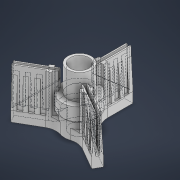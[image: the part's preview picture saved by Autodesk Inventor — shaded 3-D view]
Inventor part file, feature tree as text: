
AUTODESK INVENTOR PART (.ipt)
format: ipt  version: 2022 (Build 260153000, 153)  size: 952,320 bytes
history: native  units: in
note: dims shown in document units (in); Inventor stores cm internally (conversion verified against a paired STEP export)
features: projected_geometry x17, sketch x15, extrude x13, pattern_circular x2, chamfer x1, pattern_linear x1, plane x1, fillet x1
ambient origin geometry x8: Origin, YZ Plane, XZ Plane, XY Plane, X Axis, Y Axis, Z Axis, Center Point
bodies: Solid1 (feature_tree)
feature tree (51):
  extrude  "Extrusion1"  Depth=0.55in
  extrude  "Extrusion2"  Depth=0.125in TaperAngle=0.0deg
  extrude  "Extrusion3"  Depth=0.375in TaperAngle=0.0deg
  extrude  "Extrusion4"  Depth=0.15in
  sketch  "Sketch5"  dims[d11=0.0in d12=1.0in d13=0.0in]
  extrude  "Extrusion5"  Depth=1.0in TaperAngle=0.0deg
  chamfer  "Chamfer1"  Distance=1.0in
  sketch  "Sketch7"  dims[d17=0.08in d18=0.125in d19=45.0deg d20=1.0in]
  extrude  "Extrusion7"  Depth=1.0in
  extrude  "Extrusion8"  Depth=0.25in TaperAngle=0.0deg
  pattern_linear  "Rectangular Pattern1"  Count1=4 Spacing1=0.25in
  plane  "Work Plane1"
  fillet  "Fillet1"  Radius=0.5in
  pattern_circular  "Circular Pattern1"  Count=3 Angle=360.0deg
  extrude  "Extrusion10"  Depth=0.25in TaperAngle=0.0deg
  extrude  "Extrusion11"  Depth=0.125in
  extrude  "Extrusion12"  Depth=0.15in TaperAngle=360.0deg
  extrude  "Extrusion13"  Depth=0.25in TaperAngle=0.0deg
  sketch  "Sketch14"  dims[d56=0.3in d57=0.0in d58=0.25in d59=0.0in]
  pattern_circular  "Circular Pattern3"  [2 undecoded]
  extrude  "Extrusion14"  [1 undecoded]
  extrude  "Extrusion15"  [1 undecoded]
  sketch  "Sketch1"  dims[d0=0.69in d1=0.55in]
  sketch  "Sketch2"  dims[d2=1.0in d3=0.0in d4=0.125in d5=0.0in]
  sketch  "Sketch3"  dims[d6=0.875in d7=0.375in d8=0.0in]
  sketch  "Sketch4"  dims[d9=1.4375in d10=0.15in]
  projected_geometry  "Projected Loop1"
  sketch  "Sketch6"  dims[d14=0.0714in d15=1.0in d16=0.0in]
  projected_geometry  "Projected Loop2"
  sketch  "Sketch8"  dims[d23=0.25in d24=0.125in d25=0.0in]
  projected_geometry  "Projected Loop3"
  sketch  "Sketch9"  dims[d26=0.125in d27=0.0in d28=1.5748in d30=0.25in d37=0.5in d38=1.1811in d39=360.0deg]
  projected_geometry  "Projected Loop4"
  projected_geometry  "Projected Loop5"
  sketch  "Sketch11"  dims[d41=0.05in d42=0.0in d43=0.25in d44=0.0in]
  projected_geometry  "Projected Loop6"
  sketch  "Sketch12"  dims[d45=0.125in d46=0.0in d47=0.125in]
  projected_geometry  "Projected Loop7"
  projected_geometry  "Projected Loop8"
  projected_geometry  "Projected Loop9"
  projected_geometry  "Projected Loop10"
  projected_geometry  "Projected Loop11"
  projected_geometry  "Projected Loop12"
  sketch  "Sketch13"  dims[d48=0.15in d49=0.0in d53=1.1811in d54=360.0deg]
  projected_geometry  "Projected Loop13"
  sketch  "Sketch15"
  projected_geometry  "Projected Loop14"
  projected_geometry  "Projected Loop15"
  projected_geometry  "Projected Loop16"
  sketch  "Sketch16"
  projected_geometry  "Projected Loop17"
note: 4 required parameter values undecoded (feature->parameter linkage not recoverable at this tier; creation-order binding heuristic only, values carry confidence <= 0.55)
